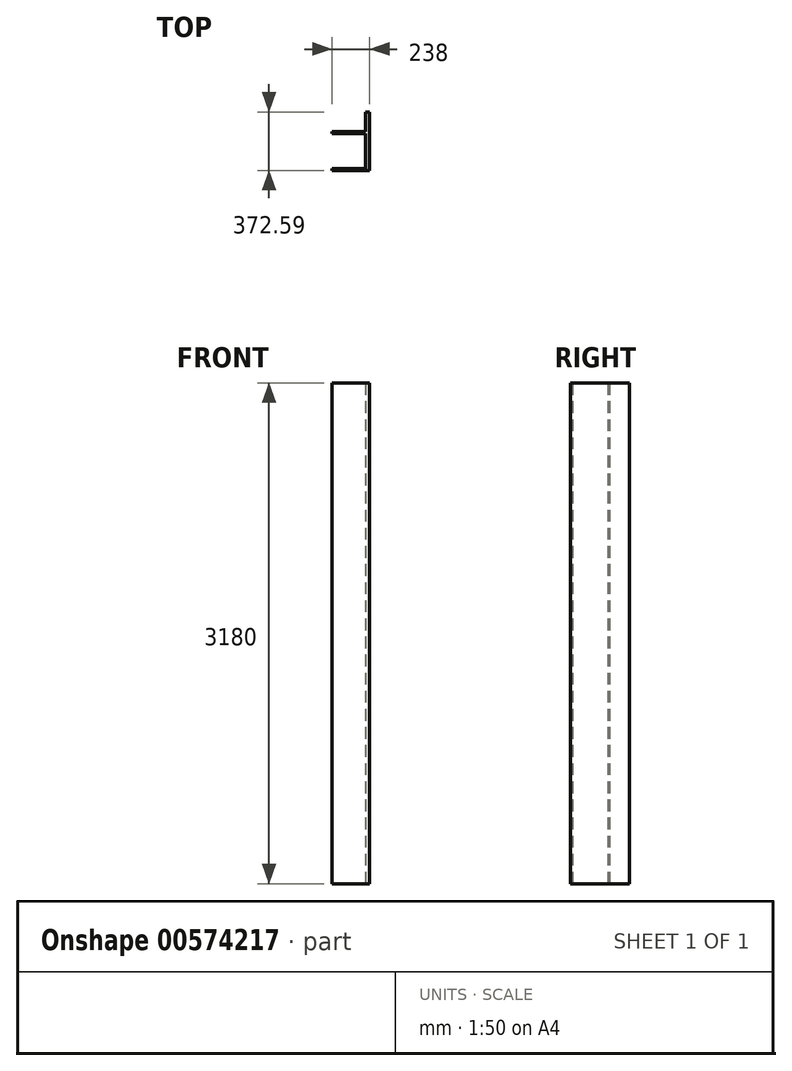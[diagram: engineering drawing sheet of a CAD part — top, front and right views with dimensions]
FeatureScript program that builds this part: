
annotation { "Feature Type Name" : "Feature", "Feature Type Description" : "" }
export const myFeature = defineFeature(function(context is Context, id is Id, definition is map)
    precondition{}
    {
        {
            var Q0;
            Q0=qCreatedBy(makeId("Top.planeOp"),FACE);
            var sketch = newSketch(context, id + "F0", { "sketchPlane" : qUnion([Q0])});
            skLineSegment(sketch, "E0", {"start": v(250, 0) * mm, "end": v(250, 372.59) * mm});
            skLineSegment(sketch, "E1", {"start": v(250, 372.59) * mm, "end": v(225, 372.59) * mm});
            skLineSegment(sketch, "E2", {"start": v(225, 372.59) * mm, "end": v(225, 247.59) * mm});
            skLineSegment(sketch, "E3", {"start": v(12, 12) * mm, "end": v(225, 12) * mm});
            skLineSegment(sketch, "E4", {"start": v(225, 12) * mm, "end": v(225, 235.59) * mm});
            skLineSegment(sketch, "E5", {"start": v(225, 235.59) * mm, "end": v(12, 235.59) * mm});
            skLineSegment(sketch, "E6", {"start": v(225, 247.59) * mm, "end": v(12, 247.59) * mm});
            skLineSegment(sketch, "E7", {"start": v(12, 247.59) * mm, "end": v(12, 235.59) * mm});
            skLineSegment(sketch, "E8", {"start": v(250, 0) * mm, "end": v(12, 0) * mm});
            skLineSegment(sketch, "E9", {"start": v(12, 0) * mm, "end": v(12, 12) * mm});
            skSolve(sketch);
        }
        {
            var Q0;
            Q0=makeQuery(id+"F0.imprint","IMPRINT",FACE,{"disambiguationData":[TD([[makeQuery(id+"F0.imprint","IMPRINT",EDGE,{"derivedFrom":sQuery(id+"F0.wireOp",EDGE,"E0")}),1.0]])]});
            extrude(context, id + "F1", {"entities" : qUnion([Q0]), "depth" : 3180 * mm, "offsetDistance" : 25 * mm});
        }
    });
